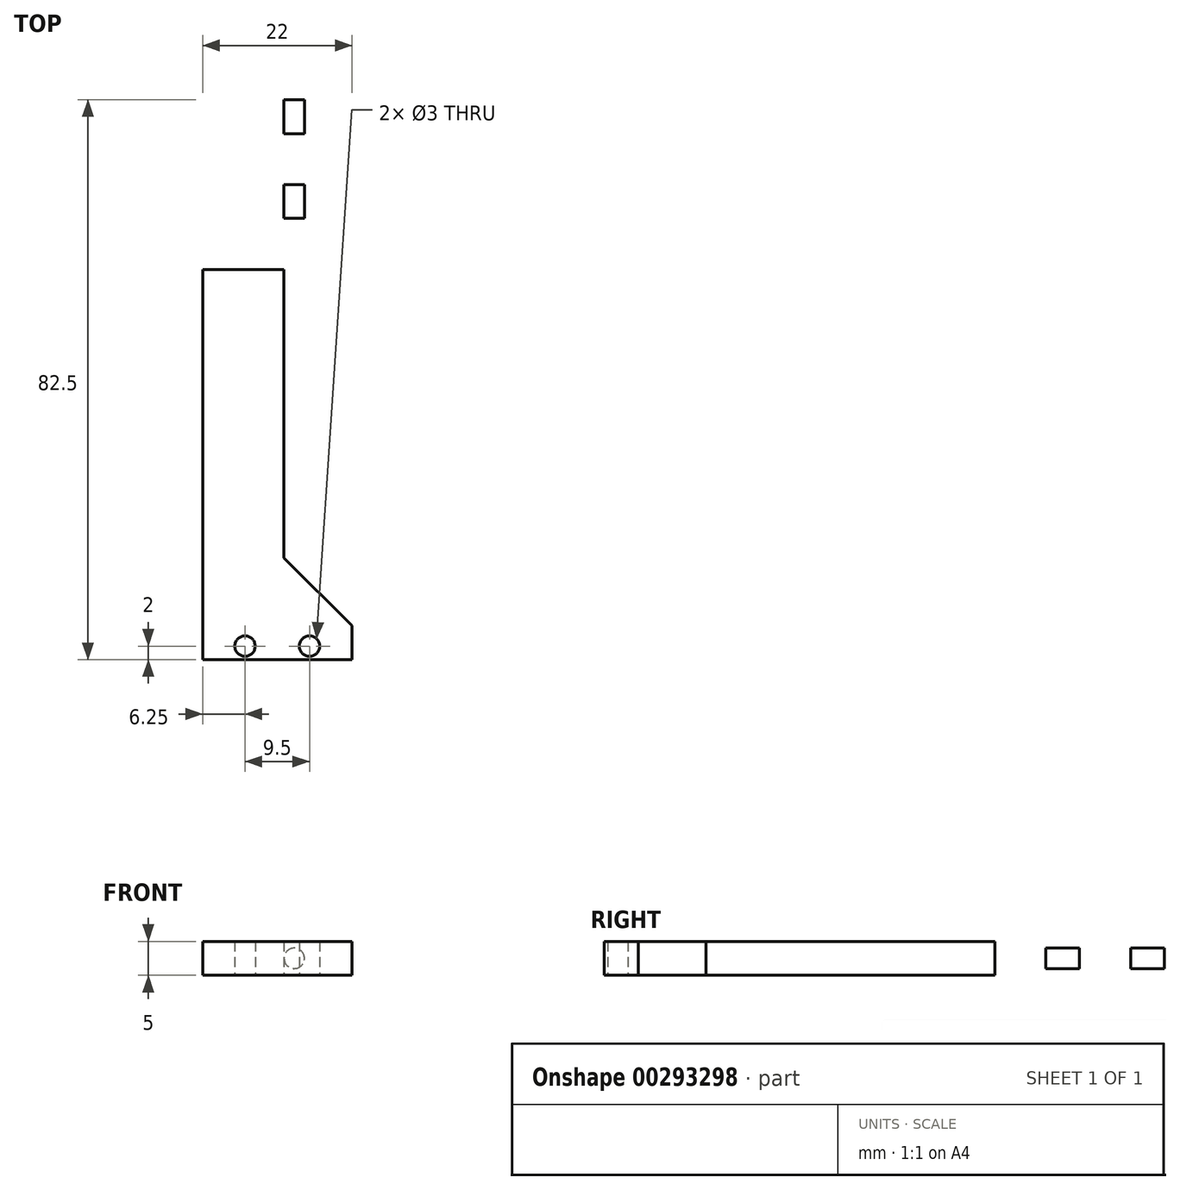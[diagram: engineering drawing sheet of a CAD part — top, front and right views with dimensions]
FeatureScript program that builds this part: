
annotation { "Feature Type Name" : "Feature", "Feature Type Description" : "" }
export const myFeature = defineFeature(function(context is Context, id is Id, definition is map)
    precondition{}
    {
        {
            var Q0;
            Q0=qCreatedBy(makeId("Top.planeOp"),FACE);
            var sketch = newSketch(context, id + "F0", { "sketchPlane" : qUnion([Q0])});
            skLineSegment(sketch, "E0", {"start": v(0, 0) * mm, "end": v(0, -75) * mm});
            skLineSegment(sketch, "E1", {"start": v(0, -75) * mm, "end": v(22, -75) * mm});
            skLineSegment(sketch, "E2", {"start": v(22, -75) * mm, "end": v(22, -60) * mm});
            skLineSegment(sketch, "E3", {"start": v(22, -60) * mm, "end": v(12, -60) * mm});
            skLineSegment(sketch, "E4", {"start": v(12, -60) * mm, "end": v(12, -10) * mm});
            skLineSegment(sketch, "E5", {"start": v(12, -10) * mm, "end": v(27, -10) * mm});
            skLineSegment(sketch, "E6", {"start": v(27, -10) * mm, "end": v(27, -5) * mm});
            skLineSegment(sketch, "E7", {"start": v(27, -5) * mm, "end": v(6, -5) * mm});
            skLineSegment(sketch, "E8", {"start": v(6, -5) * mm, "end": v(6, 2.5) * mm});
            skLineSegment(sketch, "E9", {"start": v(6, 2.5) * mm, "end": v(27, 2.5) * mm});
            skLineSegment(sketch, "E10", {"start": v(27, 2.5) * mm, "end": v(27, 7.5) * mm});
            skLineSegment(sketch, "E11", {"start": v(27, 7.5) * mm, "end": v(0, 7.5) * mm});
            skLineSegment(sketch, "E12", {"start": v(0, 7.5) * mm, "end": v(0, 0) * mm});
            skLineSegment(sketch, "E13", {"start": v(11, -75) * mm, "end": v(11, -73) * mm});
            skLineSegment(sketch, "E14", {"start": v(11, -73) * mm, "end": v(15.75, -73) * mm});
            skLineSegment(sketch, "E15", {"start": v(15.75, -73) * mm, "end": v(6.25, -73) * mm});
            skCircle(sketch, "E16", {"center": v(6.25, -73) * mm, "radius": 1.5 * mm});
            skCircle(sketch, "E17", {"center": v(15.75, -73) * mm, "radius": 1.5 * mm});
            skSolve(sketch);
        }
        {
            var Q0;
            {var subQ0=sQuery(id+"F0.wireOp",EDGE,"E0");Q0=makeQuery(id+"F0.imprint","IMPRINT",FACE,{"disambiguationData":[TD([[makeQuery(id+"F0.imprint","IMPRINT",EDGE,{"derivedFrom":subQ0}),1.0]])]});}
            extrude(context, id + "F1", {"entities" : qUnion([Q0]), "depth" : 5 * mm});
        }
        {
            var Q0;
            Q0=makeQuery(id+"F1.opExtrude","SWEPT_EDGE",EDGE,{"disambiguationData":[OSD([sQuery(id+"F0.wireOp",EDGE,"E2"),sQuery(id+"F0.wireOp",EDGE,"E3")])]});
            chamfer(context, id + "F2", {"entities" : qUnion([Q0]), "width" : 10 * mm, "tangentPropagation" : true});
        }
        {
            var Q0;
            Q0=makeQuery(id+"F1.opExtrude","SWEPT_FACE",FACE,{"disambiguationData":[OSD([sQuery(id+"F0.wireOp",EDGE,"E11")])]});
            var sketch = newSketch(context, id + "F3", { "sketchPlane" : qUnion([Q0])});
            skLineSegment(sketch, "E18", {"start": v(-27, 2.5) * mm, "end": v(0, 2.5) * mm});
            skCircle(sketch, "E19", {"center": v(-13.5, 2.5) * mm, "radius": 1.5 * mm});
            skSolve(sketch);
        }
        {
            var Q0;
            {var subQ0=sQuery(id+"F3.wireOp",EDGE,"E19");var subQ1=sQuery(id+"F3.wireOp",EDGE,"E18");var subQ2=makeQuery(id+"F3.imprint","INTERSECT",VERTEX,{"disambiguationData":[OD(0.0)],"derivedFrom":[subQ1,subQ0]});Q0=makeQuery(id+"F3.imprint","IMPRINT",FACE,{"disambiguationData":[TD([[makeQuery(id+"F3.imprint","IMPRINT",EDGE,{"disambiguationData":[TD([[subQ2,-1.0]])],"derivedFrom":subQ1}),-1.0]])]});}
            var Q1;
            {var subQ0=sQuery(id+"F3.wireOp",EDGE,"E19");var subQ1=sQuery(id+"F3.wireOp",EDGE,"E18");var subQ2=makeQuery(id+"F3.imprint","INTERSECT",VERTEX,{"disambiguationData":[OD(0.0)],"derivedFrom":[subQ1,subQ0]});Q1=makeQuery(id+"F3.imprint","IMPRINT",FACE,{"disambiguationData":[TD([[makeQuery(id+"F3.imprint","IMPRINT",EDGE,{"disambiguationData":[TD([[subQ2,-1.0]])],"derivedFrom":subQ1}),1.0]])]});}
            extrude(context, id + "F4", {"entities" : qUnion([Q0, Q1]), "operationType" : NewBodyOperationType.REMOVE, "oppositeDirection" : true, "depth" : 25 * mm});
        }
    });
